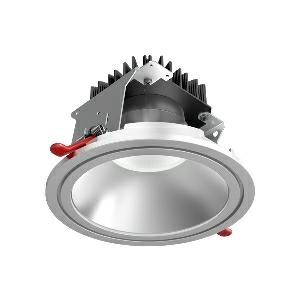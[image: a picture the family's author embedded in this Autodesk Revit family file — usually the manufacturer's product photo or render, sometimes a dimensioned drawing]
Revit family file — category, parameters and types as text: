
# Revit family: dotoo_spot_-_dse_1000_840_d_00806081_e503
name_source: partatom
category: Lighting Fixtures
units: mm (PartAtom-declared; Revit-internal decimal feet)

## family parameters
Cut with Voids When Loaded = No
Host = Face
Light Source = No
Part Type = Normal
Room Calculation Point = No
Round Connector Dimension = Use Diameter
Shared = No

## types (1)
- DOTOO.spot - DSE 1000/840/D (1 x LED, 1400 lm, 3000K)
    Apparent Load = 14 VA
    Approval mark = CE
    CIE Flux Codes = 87 99 100 100 100
    Color Rendering = 80-89
    Color Temperature = 3000K
    Control Gear = Electronic ballast
    Default Elevation = 1800 mm
    Description = DSE 1000/840/D|Recessed luminaire|light source: LED|work equipment: Electronic ballast|connected load: 220-240V, 50/60Hz|Power consumption: approx. 14 W|standby: approx. 0,20|power factor: approx. 0,900|luminous flux: 1400 lm|luminous efficacy: 100 lm/W|light distribution: Direct|direct ratio: approx. 100 %|colour temperature: Cold white, ca. 4000 K|color rendering index (CRI): >= 80|chromaticity tolerance:  3 SDCM|System of protection: IP 20|class of protection: II|technology: Continuously dimmable|operation: External|luminaire body|material: Sheet metal|colour: White|weight (net): approx. 0.7 kg|mains lead: 0.35 m Connector|Fastening: Tension spring|glare control: Prism aperture|luminance(L65): <= 2100 cd/m|unified glare rating(4H 8H): <=  19|special features: TouchDIM - dimming via standard switch, Integration into DALI light management systems, Flicker-free, Low installation depth thanks to external ballast, Suitable as emergency lighting, Ceiling installation without tools by means of tension springs, Strain relief with the possibility of through-wiring, As supplement for room depths and walking areas|
    Height = 0 mm  [stored 0 ft]
    Lamp = 1 x LED
    Lamp Light Flux = 1400 lm
    Lamp count = 1
    Length = 166 mm
    Luminous efficacy = 100 lm/W
    Manufacturer = Waldmann
    ModVariant = No
    Model = 00806081
    Mounting Place = Ceiling
    Mounting Type = Recessed
    Number of Poles = 1
    OnlyDefault = Yes
    Power Factor = 1
    Product Name = DOTOO.spot - DSE 1000/840/D
    Product group = Recessed luminaire
    ProductGroupID = 4
    Protection Class = Protection class II
    Protection Degree = IP 20
    RLX_Detail_Level = 1
    RLX_Emergency_Light_Flux = 0 lm
    RLX_Emergency_Type = 0
    RLX_Emergency_Type_DB = No
    RlxData = <blob elided: 54277 chars, md5=31bf19ef>
    Socket = socket
    Standby Power = 0 W
    System Light Flux = 1400 lm
    System Power = 14 W
    Type Comments = Product without accessories
    Type Image = 114272000-00806084.jpg
    URL = http://relux.com
    VarID = ---
    Voltage = 230 V
    Voltage Range = 220-240 V
    Weight = 0.00 kg
    Width = 0 mm  [stored 0 ft]

note: [stored X ft] marks values corroborated as IEEE doubles in the binary element streams (Revit-internal decimal feet)

## geometry (parser evidence)
native form markers: Blend x4, Sweep x13
no freeform markers — native parametric forms only
